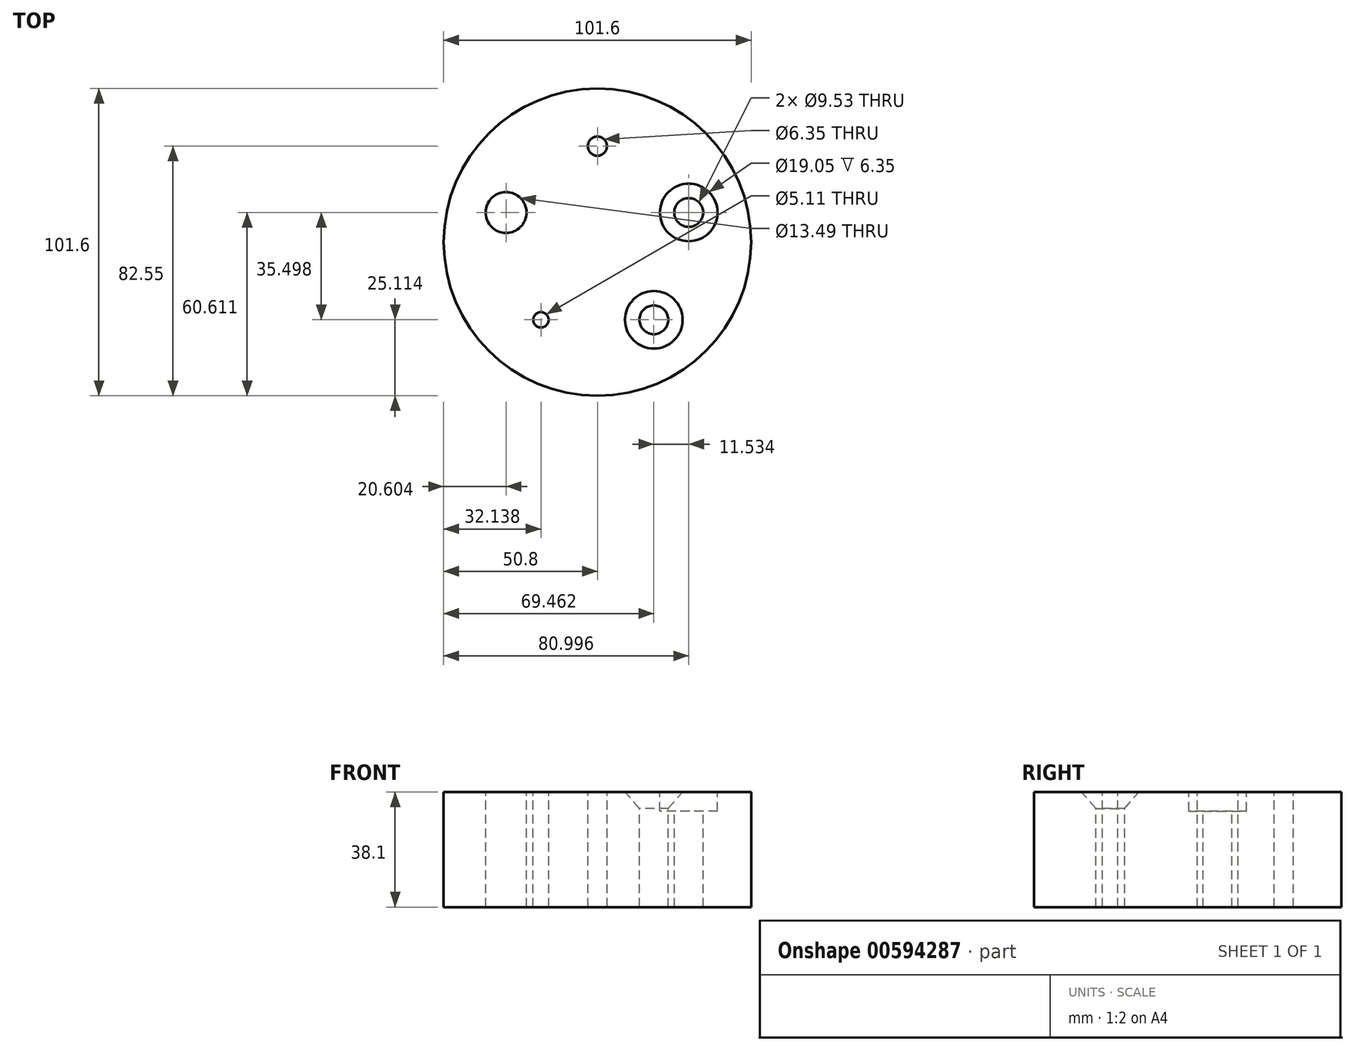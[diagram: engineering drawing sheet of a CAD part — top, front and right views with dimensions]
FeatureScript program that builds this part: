
annotation { "Feature Type Name" : "Feature", "Feature Type Description" : "" }
export const myFeature = defineFeature(function(context is Context, id is Id, definition is map)
    precondition{}
    {
        {
            var Q0;
            Q0=qCreatedBy(makeId("Top.planeOp"),FACE);
            var sketch = newSketch(context, id + "F0", { "sketchPlane" : qUnion([Q0])});
            skCircle(sketch, "E0", {"center": v(0, 0) * mm, "radius": 50.8 * mm});
            skSolve(sketch);
        }
        {
            var Q0;
            Q0 = qSketchRegion(id + "F0", true);
            extrude(context, id + "F1", {"entities" : qUnion([Q0]), "depth" : 38.1 * mm, "offsetDistance" : 25.4 * mm});
        }
        {
            var Q0;
            Q0=makeQuery(id+"F1.opExtrude","CAP_FACE",FACE,{"disambiguationData":[OSD([sQuery(id+"F0.wireOp",EDGE,"E0")])],"isStart":false});
            var sketch = newSketch(context, id + "F2", { "sketchPlane" : qUnion([Q0])});
            skCircle(sketch, "E1", {"center": v(0, 0) * mm, "radius": 31.75 * mm, "construction": true});
            skPoint(sketch, "E2", {"position": v(0, 31.75) * mm});
            skPoint(sketch, "E3.1.0", {"position": v(-30.2, 9.81) * mm});
            skPoint(sketch, "E3.2.0", {"position": v(-18.66, -25.69) * mm});
            skPoint(sketch, "E3.3.0", {"position": v(18.66, -25.69) * mm});
            skPoint(sketch, "E3.4.0", {"position": v(30.2, 9.81) * mm});
            skLineSegment(sketch, "E4", {"start": v(-30.2, 9.81) * mm, "end": v(0, 0) * mm, "construction": true});
            skLineSegment(sketch, "E5", {"start": v(0, 31.75) * mm, "end": v(0, 0) * mm, "construction": true});
            skLineSegment(sketch, "E6", {"start": v(30.2, 9.81) * mm, "end": v(0, 0) * mm, "construction": true});
            skLineSegment(sketch, "E7", {"start": v(18.66, -25.69) * mm, "end": v(0, 0) * mm, "construction": true});
            skLineSegment(sketch, "E8", {"start": v(-18.66, -25.69) * mm, "end": v(0, 0) * mm, "construction": true});
            skCircle(sketch, "E9", {"center": v(0, 31.75) * mm, "radius": 3.18 * mm});
            skCircle(sketch, "E10", {"center": v(-30.2, 9.81) * mm, "radius": 6.74 * mm});
            skCircle(sketch, "E11", {"center": v(30.2, 9.81) * mm, "radius": 4.76 * mm});
            skCircle(sketch, "E12", {"center": v(18.66, -25.69) * mm, "radius": 4.76 * mm});
            skCircle(sketch, "E13", {"center": v(-18.66, -25.69) * mm, "radius": 3.18 * mm});
            skSolve(sketch);
        }
        {
            var Q0;
            Q0=sQuery(id+"F2.wireOp",VERTEX,"E2");
            var Q1;
            Q1=makeQuery(id+"F1.opExtrude","SWEPT_BODY",BODY,{"disambiguationData":[OSD([sQuery(id+"F0.wireOp",EDGE,"E0")])]});
            hole(context, id + "F3", {"style" : HoleStyle.SIMPLE, "endStyle" : HoleEndStyle.THROUGH, "holeDiameter" : 6.35 * mm, "majorDiameter" : 6.35 * mm, "isTappedThrough" : true, "tappedDepth" : 12.7 * mm, "tapClearance" : 3, "locations" : qUnion([Q0]), "scope" : qUnion([Q1])});
        }
        {
            var Q0;
            Q0=sQuery(id+"F2.wireOp",VERTEX,"E3.4.0");
            var Q1;
            Q1=makeQuery(id+"F1.opExtrude","SWEPT_BODY",BODY,{"disambiguationData":[OSD([sQuery(id+"F0.wireOp",EDGE,"E0")])]});
            hole(context, id + "F4", {"style" : HoleStyle.C_BORE, "endStyle" : HoleEndStyle.THROUGH, "holeDiameter" : 9.52 * mm, "cBoreDiameter" : 19.05 * mm, "cBoreDepth" : 6.35 * mm, "majorDiameter" : 6.35 * mm, "isTappedThrough" : true, "tappedDepth" : 12.7 * mm, "tapClearance" : 3, "locations" : qUnion([Q0]), "scope" : qUnion([Q1])});
        }
        {
            var Q0;
            Q0=sQuery(id+"F2.wireOp",VERTEX,"E3.3.0");
            var Q1;
            Q1=makeQuery(id+"F1.opExtrude","SWEPT_BODY",BODY,{"disambiguationData":[OSD([sQuery(id+"F0.wireOp",EDGE,"E0")])]});
            hole(context, id + "F5", {"style" : HoleStyle.C_SINK, "endStyle" : HoleEndStyle.THROUGH, "holeDiameter" : 9.52 * mm, "cSinkDiameter" : 19.05 * mm, "cSinkAngle" : 82 * degree, "majorDiameter" : 6.35 * mm, "isTappedThrough" : true, "tappedDepth" : 12.7 * mm, "tapClearance" : 3, "locations" : qUnion([Q0]), "scope" : qUnion([Q1])});
        }
        {
            var Q0;
            Q0=sQuery(id+"F2.wireOp",VERTEX,"E3.2.0");
            var Q1;
            Q1=makeQuery(id+"F1.opExtrude","SWEPT_BODY",BODY,{"disambiguationData":[OSD([sQuery(id+"F0.wireOp",EDGE,"E0")])]});
            hole(context, id + "F6", {"style" : HoleStyle.SIMPLE, "endStyle" : HoleEndStyle.THROUGH, "standardTappedOrClearance" : lookupTablePath({ "standard" : "ANSI", "engagement" : "75%", "pitch" : "20 tpi", "size" : "1/4", "type" : "Tapped" }), "standardBlindInLast" : lookupTablePath({ "standard" : "ANSI", "engagement" : "75%", "pitch" : "20 tpi", "size" : "1/4", "type" : "Tapped" }), "holeDiameter" : 5.1 * mm, "majorDiameter" : 6.35 * mm, "showTappedDepth" : true, "isTappedThrough" : true, "tappedDepth" : 12.7 * mm, "tapClearance" : 3, "locations" : qUnion([Q0]), "scope" : qUnion([Q1])});
        }
        {
            var Q0;
            Q0=sQuery(id+"F2.wireOp",VERTEX,"E3.1.0");
            var Q1;
            Q1=makeQuery(id+"F1.opExtrude","SWEPT_BODY",BODY,{"disambiguationData":[OSD([sQuery(id+"F0.wireOp",EDGE,"E0")])]});
            hole(context, id + "F7", {"style" : HoleStyle.SIMPLE, "endStyle" : HoleEndStyle.THROUGH, "standardTappedOrClearance" : lookupTablePath({ "standard" : "ANSI", "fit" : "Normal (ASME)", "size" : "1/2", "type" : "Clearance" }), "standardBlindInLast" : lookupTablePath({ "fit" : "Free", "standard" : "ANSI", "size" : "1/2", "type" : "Clearance" }), "holeDiameter" : 13.5 * mm, "majorDiameter" : 6.35 * mm, "isTappedThrough" : true, "tappedDepth" : 12.7 * mm, "tapClearance" : 3, "locations" : qUnion([Q0]), "scope" : qUnion([Q1])});
        }
    });
